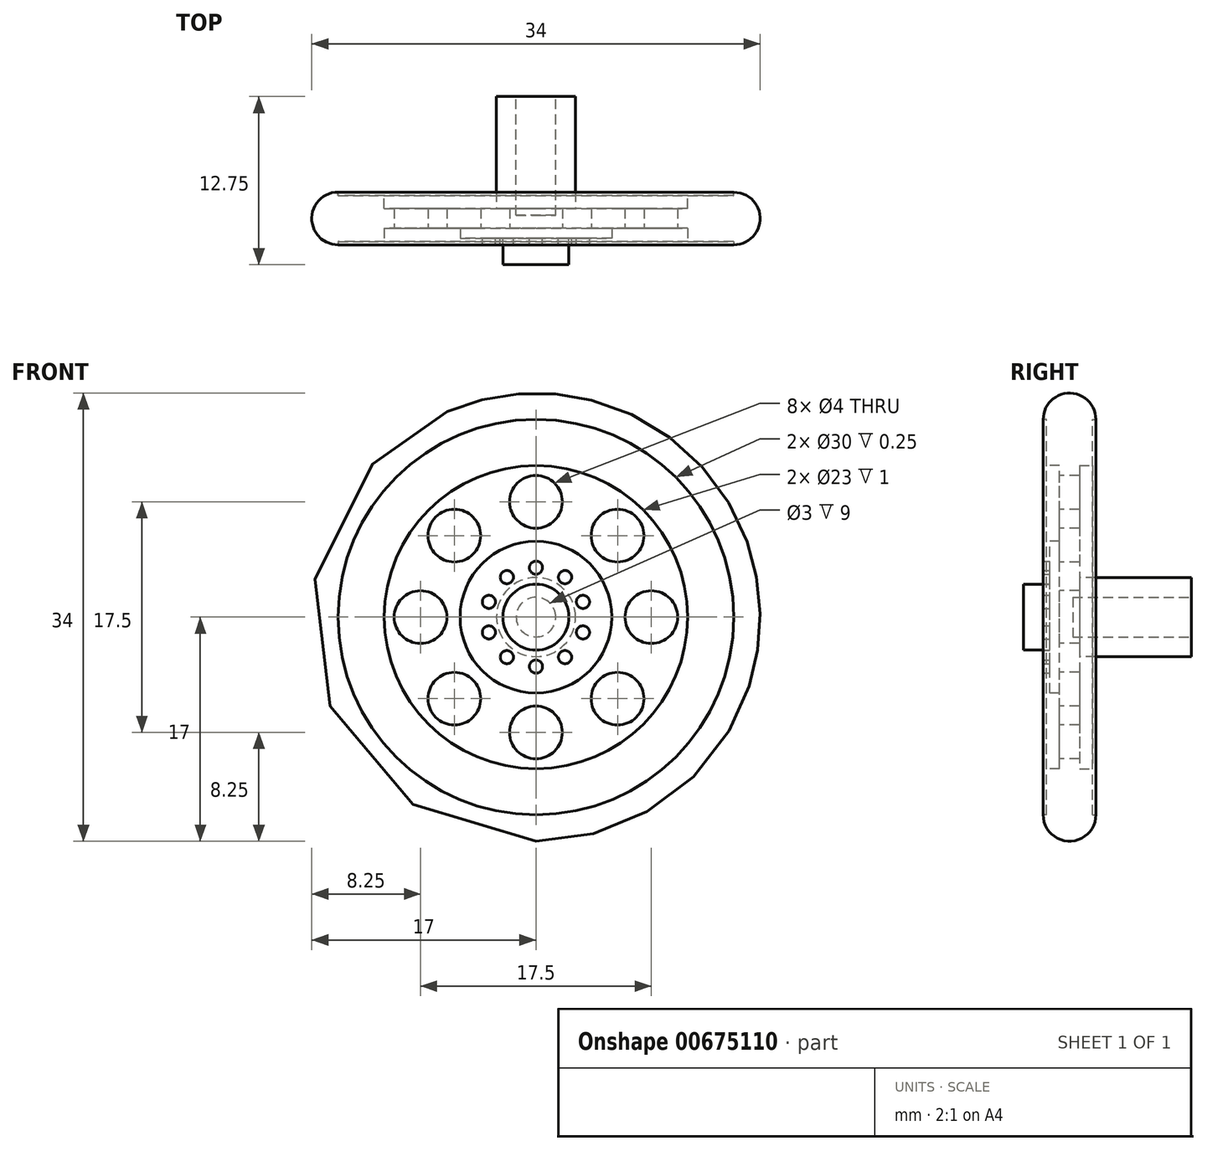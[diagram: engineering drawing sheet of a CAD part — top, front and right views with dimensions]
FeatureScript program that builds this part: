
annotation { "Feature Type Name" : "Feature", "Feature Type Description" : "" }
export const myFeature = defineFeature(function(context is Context, id is Id, definition is map)
    precondition{}
    {
        {
            var Q0;
            Q0=qCreatedBy(makeId("Front.planeOp"),FACE);
            var sketch = newSketch(context, id + "F0", { "sketchPlane" : qUnion([Q0])});
            skCircle(sketch, "E0", {"center": v(0, 0) * mm, "radius": 17 * mm});
            skSolve(sketch);
        }
        {
            var Q0;
            Q0=makeQuery(id+"F0.imprint","IMPRINT",FACE,{"disambiguationData":[TD([[makeQuery(id+"F0.imprint","IMPRINT",EDGE,{"derivedFrom":sQuery(id+"F0.wireOp",EDGE,"E0")}),1.0]])]});
            extrude(context, id + "F1", {"entities" : qUnion([Q0]), "oppositeDirection" : true, "depth" : 4 * mm, "offsetDistance" : 25 * mm});
        }
        {
            var Q0;
            Q0=makeQuery(id+"F1.opExtrude","CAP_FACE",FACE,{"disambiguationData":[OSD([sQuery(id+"F0.wireOp",EDGE,"E0")])],"isStart":true});
            fillet(context, id + "F2", {"entities" : qUnion([Q0]), "radius" : 2 * mm, "tangentPropagation" : true, "allowEdgeOverflow" : false});
        }
        {
            var Q0;
            Q0=makeQuery(id+"F1.opExtrude","CAP_FACE",FACE,{"disambiguationData":[OSD([sQuery(id+"F0.wireOp",EDGE,"E0")])],"isStart":false});
            fillet(context, id + "F3", {"entities" : qUnion([Q0]), "radius" : 2 * mm, "tangentPropagation" : true, "allowEdgeOverflow" : false});
        }
        {
            var Q0;
            Q0=makeQuery(id+"F1.opExtrude","CAP_FACE",FACE,{"disambiguationData":[OSD([sQuery(id+"F0.wireOp",EDGE,"E0")])],"isStart":true});
            var sketch = newSketch(context, id + "F4", { "sketchPlane" : qUnion([Q0])});
            skCircle(sketch, "E1", {"center": v(0, 0) * mm, "radius": 5.75 * mm});
            skCircle(sketch, "E2", {"center": v(0, 8.75) * mm, "radius": 2 * mm});
            skCircle(sketch, "E3.1.0", {"center": v(-6.19, 6.19) * mm, "radius": 2 * mm});
            skCircle(sketch, "E3.2.0", {"center": v(-8.75, 0) * mm, "radius": 2 * mm});
            skCircle(sketch, "E3.3.0", {"center": v(-6.19, -6.19) * mm, "radius": 2 * mm});
            skCircle(sketch, "E3.4.0", {"center": v(0, -8.75) * mm, "radius": 2 * mm});
            skCircle(sketch, "E3.5.0", {"center": v(6.19, -6.19) * mm, "radius": 2 * mm});
            skCircle(sketch, "E3.6.0", {"center": v(8.75, 0) * mm, "radius": 2 * mm});
            skCircle(sketch, "E3.7.0", {"center": v(6.19, 6.19) * mm, "radius": 2 * mm});
            skSolve(sketch);
        }
        {
            var Q0;
            Q0=makeQuery(id+"F4.imprint","IMPRINT",FACE,{"disambiguationData":[TD([[makeQuery(id+"F4.imprint","IMPRINT",EDGE,{"derivedFrom":sQuery(id+"F4.wireOp",EDGE,"E1")}),-1.0]])]});
            extrude(context, id + "F5", {"entities" : qUnion([Q0]), "operationType" : NewBodyOperationType.REMOVE, "oppositeDirection" : true, "depth" : .25 * mm, "offsetDistance" : 25 * mm});
        }
        {
            var Q0;
            Q0=makeQuery(id+"F1.opExtrude","CAP_FACE",FACE,{"disambiguationData":[OSD([sQuery(id+"F0.wireOp",EDGE,"E0")])],"isStart":false});
            extrude(context, id + "F6", {"entities" : qUnion([Q0]), "operationType" : NewBodyOperationType.REMOVE, "oppositeDirection" : true, "depth" : .25 * mm, "offsetDistance" : 25 * mm});
        }
        {
            var Q0;
            Q0=makeQuery(id+"F5.boolean.opBoolean","COPY",FACE,{"derivedFrom":makeQuery(id+"F5.opExtrude","CAP_FACE",FACE,{"disambiguationData":[OSD([sQuery(id+"F0.wireOp",EDGE,"E0"),sQuery(id+"F4.wireOp",EDGE,"E1"),sQuery(id+"F4.wireOp",EDGE,"E2"),sQuery(id+"F4.wireOp",EDGE,"E3.1.0"),sQuery(id+"F4.wireOp",EDGE,"E3.2.0"),sQuery(id+"F4.wireOp",EDGE,"E3.3.0"),sQuery(id+"F4.wireOp",EDGE,"E3.4.0"),sQuery(id+"F4.wireOp",EDGE,"E3.5.0"),sQuery(id+"F4.wireOp",EDGE,"E3.6.0"),sQuery(id+"F4.wireOp",EDGE,"E3.7.0")])],"isStart":false})});
            var sketch = newSketch(context, id + "F7", { "sketchPlane" : qUnion([Q0])});
            skCircle(sketch, "E4", {"center": v(0, 0) * mm, "radius": 11.5 * mm});
            skSolve(sketch);
        }
        {
            var Q0;
            Q0=makeQuery(id+"F7.imprint","IMPRINT",FACE,{"disambiguationData":[TD([[makeQuery(id+"F7.imprint","IMPRINT",EDGE,{"derivedFrom":sQuery(id+"F7.wireOp",EDGE,"E4")}),1.0]])]});
            extrude(context, id + "F8", {"entities" : qUnion([Q0]), "operationType" : NewBodyOperationType.REMOVE, "oppositeDirection" : true, "depth" : 1 * mm, "offsetDistance" : 25 * mm});
        }
        {
            var Q0;
            Q0=makeQuery(id+"F6.boolean.opBoolean","COPY",FACE,{"derivedFrom":makeQuery(id+"F6.opExtrude","CAP_FACE",FACE,{"disambiguationData":[OSD([sQuery(id+"F0.wireOp",EDGE,"E0")])],"isStart":false})});
            var sketch = newSketch(context, id + "F9", { "sketchPlane" : qUnion([Q0])});
            skCircle(sketch, "E5", {"center": v(0, 0) * mm, "radius": 11.5 * mm});
            skSolve(sketch);
        }
        {
            var Q0;
            Q0=makeQuery(id+"F9.imprint","IMPRINT",FACE,{"disambiguationData":[TD([[makeQuery(id+"F9.imprint","IMPRINT",EDGE,{"derivedFrom":sQuery(id+"F9.wireOp",EDGE,"E5")}),1.0]])]});
            extrude(context, id + "F10", {"entities" : qUnion([Q0]), "operationType" : NewBodyOperationType.REMOVE, "oppositeDirection" : true, "depth" : 1 * mm, "offsetDistance" : 25 * mm});
        }
        {
            var Q0;
            Q0=makeQuery(id+"F5.boolean.opBoolean","SPLIT",FACE,{"disambiguationData":[TD([makeQuery(id+"F5.opExtrude","SWEPT_FACE",FACE,{"disambiguationData":[OSD([sQuery(id+"F4.wireOp",EDGE,"E3.6.0")])]})])],"derivedFrom":makeQuery(id+"F1.opExtrude","CAP_FACE",FACE,{"disambiguationData":[OSD([sQuery(id+"F0.wireOp",EDGE,"E0")])],"isStart":true})});
            var Q1;
            Q1=makeQuery(id+"F5.boolean.opBoolean","SPLIT",FACE,{"disambiguationData":[TD([makeQuery(id+"F5.opExtrude","SWEPT_FACE",FACE,{"disambiguationData":[OSD([sQuery(id+"F4.wireOp",EDGE,"E3.5.0")])]})])],"derivedFrom":makeQuery(id+"F1.opExtrude","CAP_FACE",FACE,{"disambiguationData":[OSD([sQuery(id+"F0.wireOp",EDGE,"E0")])],"isStart":true})});
            var Q2;
            Q2=makeQuery(id+"F5.boolean.opBoolean","SPLIT",FACE,{"disambiguationData":[TD([makeQuery(id+"F5.opExtrude","SWEPT_FACE",FACE,{"disambiguationData":[OSD([sQuery(id+"F4.wireOp",EDGE,"E3.4.0")])]})])],"derivedFrom":makeQuery(id+"F1.opExtrude","CAP_FACE",FACE,{"disambiguationData":[OSD([sQuery(id+"F0.wireOp",EDGE,"E0")])],"isStart":true})});
            var Q3;
            Q3=makeQuery(id+"F5.boolean.opBoolean","SPLIT",FACE,{"disambiguationData":[TD([makeQuery(id+"F5.opExtrude","SWEPT_FACE",FACE,{"disambiguationData":[OSD([sQuery(id+"F4.wireOp",EDGE,"E3.2.0")])]})])],"derivedFrom":makeQuery(id+"F1.opExtrude","CAP_FACE",FACE,{"disambiguationData":[OSD([sQuery(id+"F0.wireOp",EDGE,"E0")])],"isStart":true})});
            var Q4;
            Q4=makeQuery(id+"F5.boolean.opBoolean","SPLIT",FACE,{"disambiguationData":[TD([makeQuery(id+"F5.opExtrude","SWEPT_FACE",FACE,{"disambiguationData":[OSD([sQuery(id+"F4.wireOp",EDGE,"E2")])]})])],"derivedFrom":makeQuery(id+"F1.opExtrude","CAP_FACE",FACE,{"disambiguationData":[OSD([sQuery(id+"F0.wireOp",EDGE,"E0")])],"isStart":true})});
            var Q5;
            Q5=makeQuery(id+"F5.boolean.opBoolean","SPLIT",FACE,{"disambiguationData":[TD([makeQuery(id+"F5.opExtrude","SWEPT_FACE",FACE,{"disambiguationData":[OSD([sQuery(id+"F4.wireOp",EDGE,"E3.7.0")])]})])],"derivedFrom":makeQuery(id+"F1.opExtrude","CAP_FACE",FACE,{"disambiguationData":[OSD([sQuery(id+"F0.wireOp",EDGE,"E0")])],"isStart":true})});
            var Q6;
            Q6=makeQuery(id+"F5.boolean.opBoolean","SPLIT",FACE,{"disambiguationData":[TD([makeQuery(id+"F5.opExtrude","SWEPT_FACE",FACE,{"disambiguationData":[OSD([sQuery(id+"F4.wireOp",EDGE,"E3.3.0")])]})])],"derivedFrom":makeQuery(id+"F1.opExtrude","CAP_FACE",FACE,{"disambiguationData":[OSD([sQuery(id+"F0.wireOp",EDGE,"E0")])],"isStart":true})});
            var Q7;
            Q7=makeQuery(id+"F5.boolean.opBoolean","SPLIT",FACE,{"disambiguationData":[TD([makeQuery(id+"F5.opExtrude","SWEPT_FACE",FACE,{"disambiguationData":[OSD([sQuery(id+"F4.wireOp",EDGE,"E3.1.0")])]})])],"derivedFrom":makeQuery(id+"F1.opExtrude","CAP_FACE",FACE,{"disambiguationData":[OSD([sQuery(id+"F0.wireOp",EDGE,"E0")])],"isStart":true})});
            extrude(context, id + "F11", {"entities" : qUnion([Q0, Q1, Q2, Q3, Q4, Q5, Q6, Q7]), "operationType" : NewBodyOperationType.REMOVE, "oppositeDirection" : true, "depth" : 5 * mm, "offsetDistance" : 25 * mm});
        }
        {
            var Q0;
            Q0=makeQuery(id+"F5.boolean.opBoolean","SPLIT",FACE,{"disambiguationData":[TD([makeQuery(id+"F5.opExtrude","SWEPT_FACE",FACE,{"disambiguationData":[OSD([sQuery(id+"F4.wireOp",EDGE,"E1")])]})])],"derivedFrom":makeQuery(id+"F1.opExtrude","CAP_FACE",FACE,{"disambiguationData":[OSD([sQuery(id+"F0.wireOp",EDGE,"E0")])],"isStart":true})});
            extrude(context, id + "F12", {"entities" : qUnion([Q0]), "operationType" : NewBodyOperationType.REMOVE, "oppositeDirection" : true, "depth" : .5 * mm, "offsetDistance" : 25 * mm});
        }
        {
            var Q0;
            Q0=makeQuery(id+"F12.boolean.opBoolean","COPY",FACE,{"derivedFrom":makeQuery(id+"F12.opExtrude","CAP_FACE",FACE,{"disambiguationData":[OSD([sQuery(id+"F0.wireOp",EDGE,"E0")])],"isStart":false})});
            var sketch = newSketch(context, id + "F13", { "sketchPlane" : qUnion([Q0])});
            skCircle(sketch, "E6", {"center": v(0, 0) * mm, "radius": 2.5 * mm});
            skCircle(sketch, "E7", {"center": v(0, 3.75) * mm, "radius": 0.5 * mm});
            skCircle(sketch, "E8.1.0", {"center": v(-2.2, 3.03) * mm, "radius": 0.5 * mm});
            skCircle(sketch, "E8.2.0", {"center": v(-3.57, 1.16) * mm, "radius": 0.5 * mm});
            skCircle(sketch, "E8.3.0", {"center": v(-3.57, -1.16) * mm, "radius": 0.5 * mm});
            skCircle(sketch, "E8.4.0", {"center": v(-2.2, -3.03) * mm, "radius": 0.5 * mm});
            skCircle(sketch, "E8.5.0", {"center": v(0, -3.75) * mm, "radius": 0.5 * mm});
            skCircle(sketch, "E8.6.0", {"center": v(2.2, -3.03) * mm, "radius": 0.5 * mm});
            skCircle(sketch, "E8.7.0", {"center": v(3.57, -1.16) * mm, "radius": 0.5 * mm});
            skCircle(sketch, "E8.8.0", {"center": v(3.57, 1.16) * mm, "radius": 0.5 * mm});
            skCircle(sketch, "E8.9.0", {"center": v(2.2, 3.03) * mm, "radius": 0.5 * mm});
            skSolve(sketch);
        }
        {
            var Q0;
            Q0=makeQuery(id+"F13.imprint","IMPRINT",FACE,{"disambiguationData":[TD([[makeQuery(id+"F13.imprint","IMPRINT",EDGE,{"derivedFrom":sQuery(id+"F13.wireOp",EDGE,"E8.1.0")}),1.0]])]});
            var Q1;
            Q1=makeQuery(id+"F13.imprint","IMPRINT",FACE,{"disambiguationData":[TD([[makeQuery(id+"F13.imprint","IMPRINT",EDGE,{"derivedFrom":sQuery(id+"F13.wireOp",EDGE,"E8.2.0")}),1.0]])]});
            var Q2;
            Q2=makeQuery(id+"F13.imprint","IMPRINT",FACE,{"disambiguationData":[TD([[makeQuery(id+"F13.imprint","IMPRINT",EDGE,{"derivedFrom":sQuery(id+"F13.wireOp",EDGE,"E8.3.0")}),1.0]])]});
            var Q3;
            Q3=makeQuery(id+"F13.imprint","IMPRINT",FACE,{"disambiguationData":[TD([[makeQuery(id+"F13.imprint","IMPRINT",EDGE,{"derivedFrom":sQuery(id+"F13.wireOp",EDGE,"E8.4.0")}),1.0]])]});
            var Q4;
            Q4=makeQuery(id+"F13.imprint","IMPRINT",FACE,{"disambiguationData":[TD([[makeQuery(id+"F13.imprint","IMPRINT",EDGE,{"derivedFrom":sQuery(id+"F13.wireOp",EDGE,"E8.6.0")}),1.0]])]});
            var Q5;
            Q5=makeQuery(id+"F13.imprint","IMPRINT",FACE,{"disambiguationData":[TD([[makeQuery(id+"F13.imprint","IMPRINT",EDGE,{"derivedFrom":sQuery(id+"F13.wireOp",EDGE,"E8.7.0")}),1.0]])]});
            var Q6;
            Q6=makeQuery(id+"F13.imprint","IMPRINT",FACE,{"disambiguationData":[TD([[makeQuery(id+"F13.imprint","IMPRINT",EDGE,{"derivedFrom":sQuery(id+"F13.wireOp",EDGE,"E8.8.0")}),1.0]])]});
            var Q7;
            Q7=makeQuery(id+"F13.imprint","IMPRINT",FACE,{"disambiguationData":[TD([[makeQuery(id+"F13.imprint","IMPRINT",EDGE,{"derivedFrom":sQuery(id+"F13.wireOp",EDGE,"E8.9.0")}),1.0]])]});
            var Q8;
            Q8=makeQuery(id+"F13.imprint","IMPRINT",FACE,{"disambiguationData":[TD([[makeQuery(id+"F13.imprint","IMPRINT",EDGE,{"derivedFrom":sQuery(id+"F13.wireOp",EDGE,"E7")}),1.0]])]});
            var Q9;
            Q9=makeQuery(id+"F13.imprint","IMPRINT",FACE,{"disambiguationData":[TD([[makeQuery(id+"F13.imprint","IMPRINT",EDGE,{"derivedFrom":sQuery(id+"F13.wireOp",EDGE,"E8.5.0")}),1.0]])]});
            extrude(context, id + "F14", {"entities" : qUnion([Q0, Q1, Q2, Q3, Q4, Q5, Q6, Q7, Q8, Q9]), "operationType" : NewBodyOperationType.ADD, "depth" : .5 * mm, "offsetDistance" : 25 * mm});
        }
        {
            var Q0;
            Q0=makeQuery(id+"F13.imprint","IMPRINT",FACE,{"disambiguationData":[TD([[makeQuery(id+"F13.imprint","IMPRINT",EDGE,{"derivedFrom":sQuery(id+"F13.wireOp",EDGE,"E6")}),1.0]])]});
            extrude(context, id + "F15", {"entities" : qUnion([Q0]), "operationType" : NewBodyOperationType.ADD, "depth" : 2 * mm, "offsetDistance" : 25 * mm});
        }
        {
            var Q0;
            Q0=makeQuery(id+"F10.boolean.opBoolean","COPY",FACE,{"derivedFrom":makeQuery(id+"F10.opExtrude","CAP_FACE",FACE,{"disambiguationData":[OSD([sQuery(id+"F9.wireOp",EDGE,"E5")])],"isStart":false})});
            var sketch = newSketch(context, id + "F16", { "sketchPlane" : qUnion([Q0])});
            skCircle(sketch, "E9", {"center": v(0, 0) * mm, "radius": 3 * mm});
            skSolve(sketch);
        }
        {
            var Q0;
            Q0=makeQuery(id+"F16.imprint","IMPRINT",FACE,{"disambiguationData":[TD([[makeQuery(id+"F16.imprint","IMPRINT",EDGE,{"derivedFrom":sQuery(id+"F16.wireOp",EDGE,"E9")}),1.0]])]});
            extrude(context, id + "F17", {"entities" : qUnion([Q0]), "operationType" : NewBodyOperationType.ADD, "depth" : 8.5 * mm, "offsetDistance" : 25 * mm});
        }
        {
            var Q0;
            Q0=makeQuery(id+"F17.opExtrude","CAP_FACE",FACE,{"disambiguationData":[OSD([sQuery(id+"F16.wireOp",EDGE,"E9")])],"isStart":false});
            var sketch = newSketch(context, id + "F18", { "sketchPlane" : qUnion([Q0])});
            skCircle(sketch, "E10", {"center": v(0, 0) * mm, "radius": 1.5 * mm});
            skSolve(sketch);
        }
        {
            var Q0;
            Q0=makeQuery(id+"F18.imprint","IMPRINT",FACE,{"disambiguationData":[TD([[makeQuery(id+"F18.imprint","IMPRINT",EDGE,{"derivedFrom":sQuery(id+"F18.wireOp",EDGE,"E10")}),1.0]])]});
            extrude(context, id + "F19", {"entities" : qUnion([Q0]), "operationType" : NewBodyOperationType.REMOVE, "oppositeDirection" : true, "depth" : 9 * mm, "offsetDistance" : 25 * mm});
        }
    });
